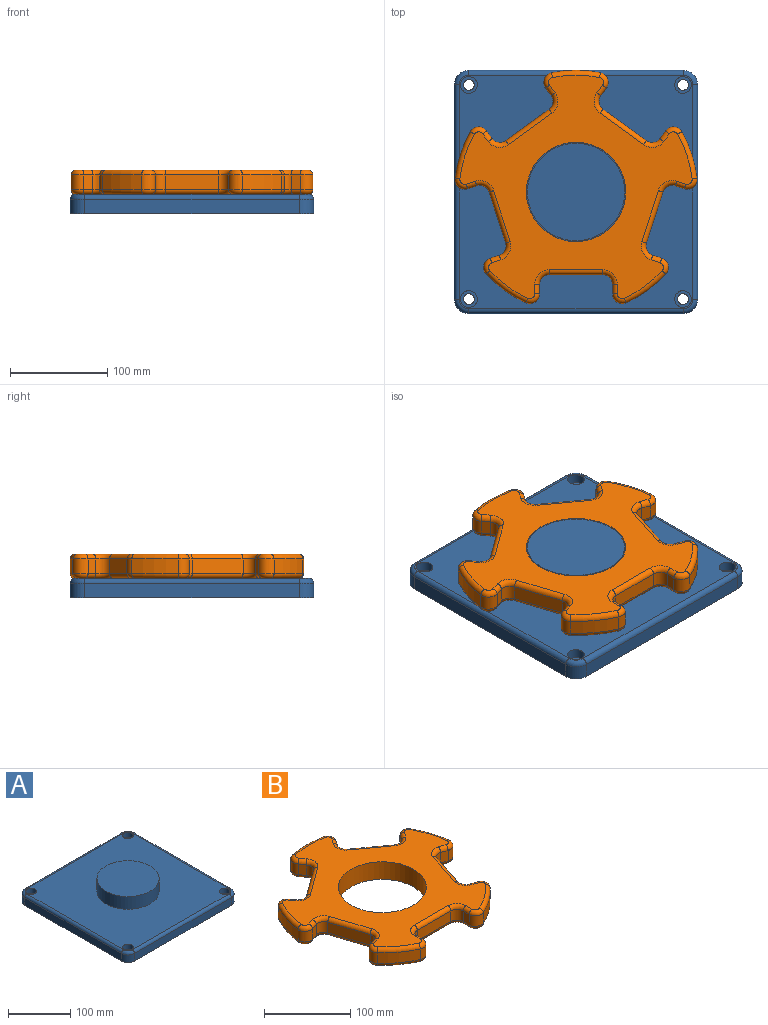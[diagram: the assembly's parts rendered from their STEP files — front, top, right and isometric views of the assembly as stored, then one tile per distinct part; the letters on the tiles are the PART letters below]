
ASSEMBLY  parts=2 mates=1
PART A: 32 faces, bbox 252.5x252.5x45 mm
  f0: plane 220x15mm, normal (1,0,0), area 3300mm2, adj f5,f8,f11,f27
  f1: plane 220x15mm, normal (0,1,0), area 3300mm2, adj f5,f8,f9,f31
  f2: plane 220x15mm, normal (-1,0,0), area 3300mm2, adj f5,f9,f10,f28
  f3: plane 220x15mm, normal (0,-1,0), area 3300mm2, adj f5,f10,f11,f24
  f4: plane 240x240mm, normal (0,0,1), area 48725.4mm2, adj f6,f14,f17,f20,f23,f24,f25,f26
  f5: plane 250x250mm, normal (0,0,-1), area 61926.7mm2, adj f0,f1,f2,f3,f8,f9,f10,f11
  f6: cylinder r=50mm len=100mm, axis (0,0,-1), area 7854mm2, adj f4,f7
  f7: plane 100x100mm, normal (0,0,1), area 7854mm2, adj f6
  f8: cylinder r=15mm len=15mm, axis (0,0,-1), area 353.4mm2, adj f0,f1,f5,f29
  f9: cylinder r=15mm len=15mm, axis (0,0,1), area 353.4mm2, adj f1,f2,f5,f30
  f10: cylinder r=15mm len=15mm, axis (0,0,-1), area 353.4mm2, adj f2,f3,f5,f26
  f11: cylinder r=15mm len=15mm, axis (0,0,1), area 353.4mm2, adj f0,f3,f5,f25
  f12: cylinder r=5.5mm len=11mm, axis (0,0,1), area 345.6mm2, adj f5,f13
  f13: plane 17.25x17.25mm, normal (0,0,1), area 138.7mm2, adj f12,f14
  f14: cylinder r=8.62mm len=17.25mm, axis (0,0,1), area 541.9mm2, adj f4,f13
  f15: cylinder r=5.5mm len=11mm, axis (0,0,1), area 345.6mm2, adj f5,f16
  f16: plane 17.25x17.25mm, normal (0,0,1), area 138.7mm2, adj f15,f17
  f17: cylinder r=8.62mm len=17.25mm, axis (0,0,1), area 541.9mm2, adj f4,f16
  f18: cylinder r=5.5mm len=11mm, axis (0,0,1), area 345.6mm2, adj f5,f19
  f19: plane 17.25x17.25mm, normal (0,0,1), area 138.7mm2, adj f18,f20
  f20: cylinder r=8.62mm len=17.25mm, axis (0,0,1), area 541.9mm2, adj f4,f19
  f21: cylinder r=5.5mm len=11mm, axis (0,0,1), area 345.6mm2, adj f5,f22
  f22: plane 17.25x17.25mm, normal (0,0,1), area 138.7mm2, adj f21,f23
  f23: cylinder r=8.62mm len=17.25mm, axis (0,0,1), area 541.9mm2, adj f4,f22
  f24: cylinder r=5mm len=220mm, axis (-1,0,0), area 1727.9mm2, adj f3,f4,f25,f26
  f25: torus R=10mm, axis (0,0,1), area 162.6mm2, adj f4,f11,f24,f27
  f26: torus R=10mm, axis (0,0,1), area 162.6mm2, adj f4,f10,f24,f28
  f27: cylinder r=5mm len=220mm, axis (0,-1,0), area 1727.9mm2, adj f0,f4,f25,f29
  f28: cylinder r=5mm len=220mm, axis (0,1,0), area 1727.9mm2, adj f2,f4,f26,f30
  f29: torus R=10mm, axis (0,0,1), area 162.6mm2, adj f4,f8,f27,f31
  f30: torus R=10mm, axis (0,0,1), area 162.6mm2, adj f4,f9,f28,f31
  f31: cylinder r=5mm len=220mm, axis (1,0,0), area 1727.9mm2, adj f1,f4,f29,f30
PART B: 123 faces, bbox 268.9x258.5x25 mm
  f0: plane 238.57x229.73mm, normal (0,0,1), area 21505.7mm2, adj f6,f43,f44,f45,f46,f47,f48,f49
  f1: plane 238.57x229.73mm, normal (0,0,-1), area 21505.7mm2, adj f6,f83,f84,f85,f86,f87,f88,f89
  f2: cylinder r=125mm len=40.68mm, axis (0,0,-1), area 759.5mm2, adj f13,f42,f51,f91
  f3: cylinder r=125mm len=47.82mm, axis (0,0,-1), area 759.5mm2, adj f35,f41,f67,f107
  f4: cylinder r=125mm len=50.29mm, axis (0,0,-1), area 759.5mm2, adj f28,f34,f82,f122
  f5: cylinder r=125mm len=47.82mm, axis (0,0,-1), area 759.5mm2, adj f21,f27,f66,f106
  f6: cylinder r=51mm len=102mm, axis (0,0,-1), area 8011.1mm2, adj f0,f1
  f7: cylinder r=125mm len=40.68mm, axis (0,0,-1), area 759.5mm2, adj f14,f20,f50,f90
  f8: plane 15x9.73mm, normal (-1,0,0), area 146mm2, adj f11,f14,f46,f86
  f9: plane 55x15mm, normal (0,-1,0), area 825mm2, adj f11,f12,f43,f83
  f10: plane 15x9.73mm, normal (1,0,0), area 146mm2, adj f12,f13,f47,f87
  f11: cylinder r=10mm len=15mm, axis (0,0,-1), area 235.6mm2, adj f8,f9,f44,f84
  f12: cylinder r=10mm len=15mm, axis (0,0,-1), area 235.6mm2, adj f9,f10,f45,f85
  f13: cylinder r=10mm len=15mm, axis (0,0,-1), area 299.5mm2, adj f2,f10,f49,f89
  f14: cylinder r=10mm len=15mm, axis (0,0,-1), area 299.5mm2, adj f7,f8,f48,f88
  f15: plane 15x9.26mm, normal (-0.31,-0.95,0), area 146mm2, adj f18,f21,f62,f102
  f16: plane 52.31x17mm, normal (0.95,-0.31,0), area 825mm2, adj f18,f19,f58,f98
  f17: plane 15x9.26mm, normal (0.31,0.95,0), area 146mm2, adj f19,f20,f54,f94
  f18: cylinder r=10mm len=15mm, axis (0,0,-1), area 235.6mm2, adj f15,f16,f60,f100
  f19: cylinder r=10mm len=15mm, axis (0,0,-1), area 235.6mm2, adj f16,f17,f56,f96
  f20: cylinder r=10mm len=16.25mm, axis (0,0,-1), area 299.5mm2, adj f7,f17,f52,f92
  f21: cylinder r=10mm len=15mm, axis (0,0,-1), area 299.5mm2, adj f5,f15,f64,f104
  f22: plane 15x7.87mm, normal (0.81,-0.59,0), area 146mm2, adj f25,f28,f78,f118
  f23: plane 44.5x32.33mm, normal (0.59,0.81,0), area 825mm2, adj f25,f26,f74,f114
  f24: plane 15x7.87mm, normal (-0.81,0.59,0), area 146mm2, adj f26,f27,f70,f110
  f25: cylinder r=10mm len=15mm, axis (0,0,-1), area 235.6mm2, adj f22,f23,f76,f116
  f26: cylinder r=10mm len=15mm, axis (0,0,-1), area 235.6mm2, adj f23,f24,f72,f112
  f27: cylinder r=10mm len=16.78mm, axis (0,0,-1), area 299.5mm2, adj f5,f24,f68,f108
  f28: cylinder r=10mm len=15.67mm, axis (0,0,-1), area 299.5mm2, adj f4,f22,f80,f120
  f29: plane 15x7.87mm, normal (0.81,0.59,0), area 146mm2, adj f32,f35,f71,f111
  f30: plane 44.5x32.33mm, normal (-0.59,0.81,0), area 825mm2, adj f32,f33,f75,f115
  f31: plane 15x7.87mm, normal (-0.81,-0.59,0), area 146mm2, adj f33,f34,f79,f119
  f32: cylinder r=10mm len=15mm, axis (0,0,-1), area 235.6mm2, adj f29,f30,f73,f113
  f33: cylinder r=10mm len=15mm, axis (0,0,-1), area 235.6mm2, adj f30,f31,f77,f117
  f34: cylinder r=10mm len=15.67mm, axis (0,0,-1), area 299.5mm2, adj f4,f31,f81,f121
  f35: cylinder r=10mm len=16.78mm, axis (0,0,-1), area 299.5mm2, adj f3,f29,f69,f109
  f36: plane 15x9.26mm, normal (-0.31,0.95,0), area 146mm2, adj f39,f42,f55,f95
  f37: plane 52.31x17mm, normal (-0.95,-0.31,0), area 825mm2, adj f39,f40,f59,f99
  f38: plane 15x9.26mm, normal (0.31,-0.95,0), area 146mm2, adj f40,f41,f63,f103
  f39: cylinder r=10mm len=15mm, axis (0,0,-1), area 235.6mm2, adj f36,f37,f57,f97
  f40: cylinder r=10mm len=15mm, axis (0,0,-1), area 235.6mm2, adj f37,f38,f61,f101
  f41: cylinder r=10mm len=15mm, axis (0,0,-1), area 299.5mm2, adj f3,f38,f65,f105
  f42: cylinder r=10mm len=16.25mm, axis (0,0,-1), area 299.5mm2, adj f2,f36,f53,f93
  f43: cylinder r=5mm len=55mm, axis (1,0,0), area 432mm2, adj f0,f9,f44,f45
  f44: torus R=15mm, axis (0,0,1), area 145.8mm2, adj f0,f11,f43,f46
  f45: torus R=15mm, axis (0,0,1), area 145.8mm2, adj f0,f12,f43,f47
  f46: cylinder r=5mm len=9.73mm, axis (0,-1,0), area 76.4mm2, adj f0,f8,f44,f48
  f47: cylinder r=5mm len=9.73mm, axis (0,1,0), area 76.4mm2, adj f0,f10,f45,f49
  f48: torus R=5mm, axis (0,0,1), area 128.3mm2, adj f0,f14,f46,f50
  f49: torus R=5mm, axis (0,0,1), area 128.3mm2, adj f0,f13,f47,f51
  f50: torus R=120mm, axis (0,0,1), area 391.9mm2, adj f0,f7,f48,f52
  f51: torus R=120mm, axis (0,0,1), area 391.9mm2, adj f0,f2,f49,f53
  f52: torus R=5mm, axis (0,0,1), area 128.3mm2, adj f0,f20,f50,f54
  f53: torus R=5mm, axis (0,0,1), area 128.3mm2, adj f0,f42,f51,f55
  f54: cylinder r=5mm len=10.8mm, axis (-0.95,0.31,0), area 76.4mm2, adj f0,f17,f52,f56
  f55: cylinder r=5mm len=10.8mm, axis (-0.95,-0.31,0), area 76.4mm2, adj f0,f36,f53,f57
  f56: torus R=15mm, axis (0,0,1), area 145.8mm2, adj f0,f19,f54,f58
  f57: torus R=15mm, axis (0,0,1), area 145.8mm2, adj f0,f39,f55,f59
  f58: cylinder r=5mm len=53.85mm, axis (0.31,0.95,0), area 432mm2, adj f0,f16,f56,f60
  f59: cylinder r=5mm len=53.85mm, axis (0.31,-0.95,0), area 432mm2, adj f0,f37,f57,f61
  f60: torus R=15mm, axis (0,0,1), area 145.8mm2, adj f0,f18,f58,f62
  f61: torus R=15mm, axis (0,0,1), area 145.8mm2, adj f0,f40,f59,f63
  f62: cylinder r=5mm len=10.8mm, axis (0.95,-0.31,0), area 76.4mm2, adj f0,f15,f60,f64
  f63: cylinder r=5mm len=10.8mm, axis (0.95,0.31,0), area 76.4mm2, adj f0,f38,f61,f65
  f64: torus R=5mm, axis (0,0,1), area 128.3mm2, adj f0,f21,f62,f66
  f65: torus R=5mm, axis (0,0,1), area 128.3mm2, adj f0,f41,f63,f67
  f66: torus R=120mm, axis (0,0,1), area 391.9mm2, adj f0,f5,f64,f68
  f67: torus R=120mm, axis (0,0,1), area 391.9mm2, adj f0,f3,f65,f69
  f68: torus R=5mm, axis (0,0,1), area 128.3mm2, adj f0,f27,f66,f70
  f69: torus R=5mm, axis (0,0,1), area 128.3mm2, adj f0,f35,f67,f71
  f70: cylinder r=5mm len=10.81mm, axis (-0.59,-0.81,0), area 76.4mm2, adj f0,f24,f68,f72
  f71: cylinder r=5mm len=10.81mm, axis (-0.59,0.81,0), area 76.4mm2, adj f0,f29,f69,f73
  f72: torus R=15mm, axis (0,0,1), area 145.8mm2, adj f0,f26,f70,f74
  f73: torus R=15mm, axis (0,0,1), area 145.8mm2, adj f0,f32,f71,f75
  f74: cylinder r=5mm len=47.44mm, axis (-0.81,0.59,0), area 432mm2, adj f0,f23,f72,f76
  f75: cylinder r=5mm len=47.44mm, axis (-0.81,-0.59,0), area 432mm2, adj f0,f30,f73,f77
  f76: torus R=15mm, axis (0,0,1), area 145.8mm2, adj f0,f25,f74,f78
  f77: torus R=15mm, axis (0,0,1), area 145.8mm2, adj f0,f33,f75,f79
  f78: cylinder r=5mm len=10.81mm, axis (0.59,0.81,0), area 76.4mm2, adj f0,f22,f76,f80
  f79: cylinder r=5mm len=10.81mm, axis (0.59,-0.81,0), area 76.4mm2, adj f0,f31,f77,f81
  f80: torus R=5mm, axis (0,0,1), area 128.3mm2, adj f0,f28,f78,f82
  f81: torus R=5mm, axis (0,0,1), area 128.3mm2, adj f0,f34,f79,f82
  f82: torus R=120mm, axis (0,0,1), area 391.9mm2, adj f0,f4,f80,f81
  f83: cylinder r=5mm len=55mm, axis (-1,0,0), area 432mm2, adj f1,f9,f84,f85
  f84: torus R=15mm, axis (0,0,1), area 145.8mm2, adj f1,f11,f83,f86
  f85: torus R=15mm, axis (0,0,1), area 145.8mm2, adj f1,f12,f83,f87
  f86: cylinder r=5mm len=9.73mm, axis (0,1,0), area 76.4mm2, adj f1,f8,f84,f88
  f87: cylinder r=5mm len=9.73mm, axis (0,-1,0), area 76.4mm2, adj f1,f10,f85,f89
  f88: torus R=5mm, axis (0,0,1), area 128.3mm2, adj f1,f14,f86,f90
  f89: torus R=5mm, axis (0,0,1), area 128.3mm2, adj f1,f13,f87,f91
  f90: torus R=120mm, axis (0,0,1), area 391.9mm2, adj f1,f7,f88,f92
  f91: torus R=120mm, axis (0,0,1), area 391.9mm2, adj f1,f2,f89,f93
  f92: torus R=5mm, axis (0,0,1), area 128.3mm2, adj f1,f20,f90,f94
  f93: torus R=5mm, axis (0,0,1), area 128.3mm2, adj f1,f42,f91,f95
  f94: cylinder r=5mm len=10.8mm, axis (0.95,-0.31,0), area 76.4mm2, adj f1,f17,f92,f96
  f95: cylinder r=5mm len=10.8mm, axis (0.95,0.31,0), area 76.4mm2, adj f1,f36,f93,f97
  f96: torus R=15mm, axis (0,0,1), area 145.8mm2, adj f1,f19,f94,f98
  f97: torus R=15mm, axis (0,0,1), area 145.8mm2, adj f1,f39,f95,f99
  f98: cylinder r=5mm len=53.85mm, axis (-0.31,-0.95,0), area 432mm2, adj f1,f16,f96,f100
  f99: cylinder r=5mm len=53.85mm, axis (-0.31,0.95,0), area 432mm2, adj f1,f37,f97,f101
  f100: torus R=15mm, axis (0,0,1), area 145.8mm2, adj f1,f18,f98,f102
  f101: torus R=15mm, axis (0,0,1), area 145.8mm2, adj f1,f40,f99,f103
  f102: cylinder r=5mm len=10.8mm, axis (-0.95,0.31,0), area 76.4mm2, adj f1,f15,f100,f104
  f103: cylinder r=5mm len=10.8mm, axis (-0.95,-0.31,0), area 76.4mm2, adj f1,f38,f101,f105
  f104: torus R=5mm, axis (0,0,1), area 128.3mm2, adj f1,f21,f102,f106
  f105: torus R=5mm, axis (0,0,1), area 128.3mm2, adj f1,f41,f103,f107
  f106: torus R=120mm, axis (0,0,1), area 391.9mm2, adj f1,f5,f104,f108
  f107: torus R=120mm, axis (0,0,1), area 391.9mm2, adj f1,f3,f105,f109
  f108: torus R=5mm, axis (0,0,1), area 128.3mm2, adj f1,f27,f106,f110
  f109: torus R=5mm, axis (0,0,1), area 128.3mm2, adj f1,f35,f107,f111
  f110: cylinder r=5mm len=10.81mm, axis (0.59,0.81,0), area 76.4mm2, adj f1,f24,f108,f112
  f111: cylinder r=5mm len=10.81mm, axis (0.59,-0.81,0), area 76.4mm2, adj f1,f29,f109,f113
  f112: torus R=15mm, axis (0,0,1), area 145.8mm2, adj f1,f26,f110,f114
  f113: torus R=15mm, axis (0,0,1), area 145.8mm2, adj f1,f32,f111,f115
  f114: cylinder r=5mm len=47.44mm, axis (0.81,-0.59,0), area 432mm2, adj f1,f23,f112,f116
  f115: cylinder r=5mm len=47.44mm, axis (0.81,0.59,0), area 432mm2, adj f1,f30,f113,f117
  f116: torus R=15mm, axis (0,0,1), area 145.8mm2, adj f1,f25,f114,f118
  f117: torus R=15mm, axis (0,0,1), area 145.8mm2, adj f1,f33,f115,f119
  f118: cylinder r=5mm len=10.81mm, axis (-0.59,-0.81,0), area 76.4mm2, adj f1,f22,f116,f120
  f119: cylinder r=5mm len=10.81mm, axis (-0.59,0.81,0), area 76.4mm2, adj f1,f31,f117,f121
  f120: torus R=5mm, axis (0,0,1), area 128.3mm2, adj f1,f28,f118,f122
  f121: torus R=5mm, axis (0,0,1), area 128.3mm2, adj f1,f34,f119,f122
  f122: torus R=120mm, axis (0,0,1), area 391.9mm2, adj f1,f4,f120,f121
PLACE A at identity fixed
PLACE B at identity
MATE revolute B.f2 <-> A.f6  axis (0,0,-1) through (0,0,32.5)mm
